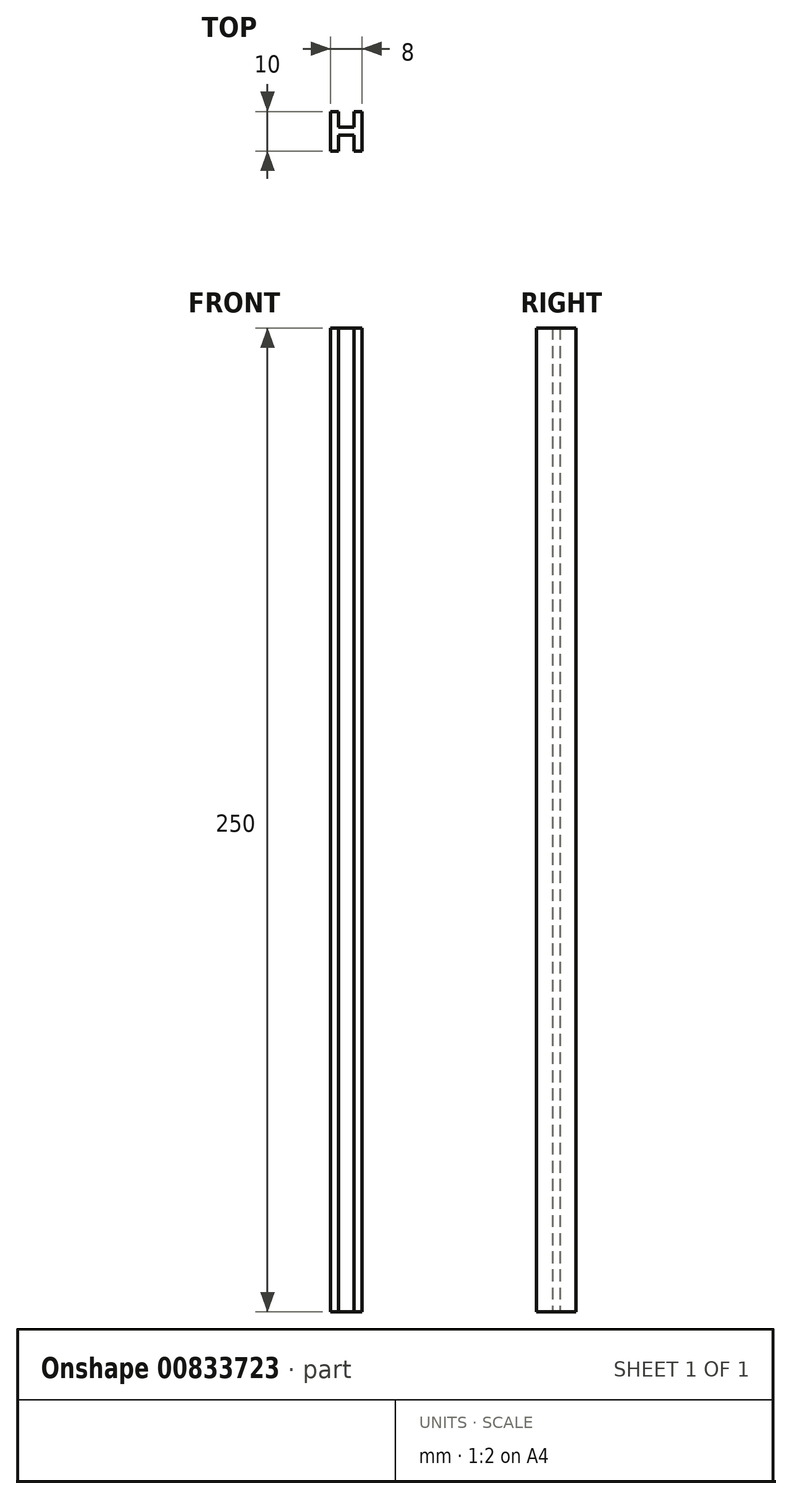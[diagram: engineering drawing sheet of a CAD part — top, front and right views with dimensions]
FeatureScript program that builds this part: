
annotation { "Feature Type Name" : "Feature", "Feature Type Description" : "" }
export const myFeature = defineFeature(function(context is Context, id is Id, definition is map)
    precondition{}
    {
        {
            var Q0;
            Q0=qCreatedBy(makeId("Top.planeOp"),FACE);
            var sketch = newSketch(context, id + "F0", { "sketchPlane" : qUnion([Q0])});
            skLineSegment(sketch, "E0", {"start": v(-26.8, 10) * mm, "end": v(-26.8, 0) * mm});
            skLineSegment(sketch, "E1", {"start": v(-26.8, 10) * mm, "end": v(-24.8, 10) * mm});
            skLineSegment(sketch, "E2", {"start": v(-26.8, 0) * mm, "end": v(-24.8, 0) * mm});
            skLineSegment(sketch, "E3", {"start": v(-24.8, 10) * mm, "end": v(-24.8, 6) * mm});
            skLineSegment(sketch, "E4", {"start": v(-24.8, 6) * mm, "end": v(-20.8, 6) * mm});
            skLineSegment(sketch, "E5", {"start": v(-20.8, 6) * mm, "end": v(-20.8, 10) * mm});
            skLineSegment(sketch, "E6", {"start": v(-20.8, 10) * mm, "end": v(-18.8, 10) * mm});
            skLineSegment(sketch, "E7", {"start": v(-24.8, 0) * mm, "end": v(-24.8, 4) * mm});
            skLineSegment(sketch, "E8", {"start": v(-24.8, 4) * mm, "end": v(-20.8, 4) * mm});
            skLineSegment(sketch, "E9", {"start": v(-20.8, 4) * mm, "end": v(-20.8, 0) * mm});
            skLineSegment(sketch, "E10", {"start": v(-20.8, 0) * mm, "end": v(-18.8, 0) * mm});
            skLineSegment(sketch, "E11", {"start": v(-18.8, 10) * mm, "end": v(-18.8, 0) * mm});
            skSolve(sketch);
        }
        {
            var Q0;
            Q0=makeQuery(id+"F0.imprint","IMPRINT",FACE,{"disambiguationData":[TD([[makeQuery(id+"F0.imprint","IMPRINT",EDGE,{"derivedFrom":sQuery(id+"F0.wireOp",EDGE,"E0")}),1.0]])]});
            extrude(context, id + "F1", {"entities" : qUnion([Q0]), "depth" : 250 * mm, "offsetDistance" : 25 * mm});
        }
    });
